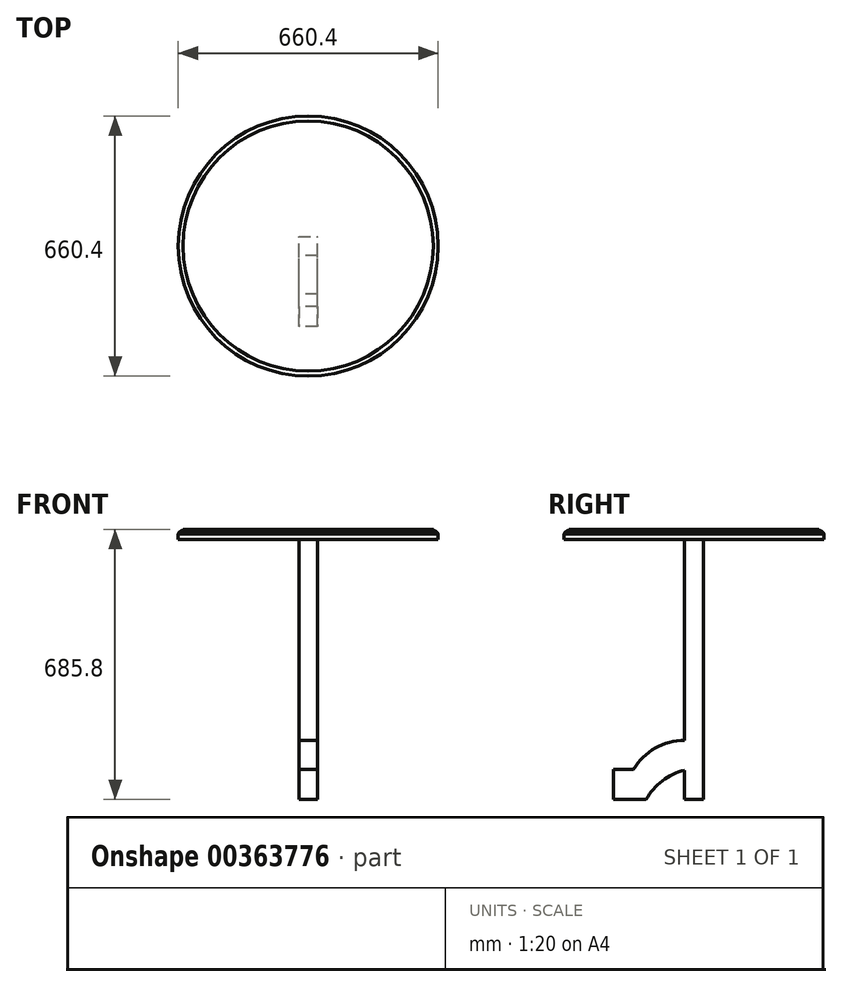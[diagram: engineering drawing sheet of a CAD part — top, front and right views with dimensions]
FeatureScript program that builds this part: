
annotation { "Feature Type Name" : "Feature", "Feature Type Description" : "" }
export const myFeature = defineFeature(function(context is Context, id is Id, definition is map)
    precondition{}
    {
        {
            var Q0;
            Q0=qCreatedBy(makeId("Top.planeOp"),FACE);
            var sketch = newSketch(context, id + "F0", { "sketchPlane" : qUnion([Q0])});
            skCircle(sketch, "E0", {"center": v(0, 0) * mm, "radius": 330.2 * mm});
            skSolve(sketch);
        }
        {
            var Q0;
            Q0=makeQuery(id+"F0.imprint","IMPRINT",FACE,{"disambiguationData":[TD([[makeQuery(id+"F0.imprint","IMPRINT",EDGE,{"derivedFrom":sQuery(id+"F0.wireOp",EDGE,"E0")}),1.0]])]});
            extrude(context, id + "F1", {"entities" : qUnion([Q0]), "depth" : 25.4 * mm});
        }
        {
            var Q0;
            Q0=qCreatedBy(makeId("Front.planeOp"),FACE);
            var sketch = newSketch(context, id + "F2", { "sketchPlane" : qUnion([Q0])});
            skLineSegment(sketch, "E1", {"start": v(-317.8, 25.4) * mm, "end": v(-317.8, 22.86) * mm});
            skArc(sketch, "E2", {"start": v(-317.8, 22.86) * mm, "mid": v(-325.99, 20.08) * mm, "end": v(-330.5, 12.7) * mm});
            skLineSegment(sketch, "E3", {"start": v(-330.5, 12.7) * mm, "end": v(-330.5, 25.4) * mm});
            skLineSegment(sketch, "E4", {"start": v(-330.5, 25.4) * mm, "end": v(-317.8, 25.4) * mm});
            skLineSegment(sketch, "E5", {"start": v(0, 84.6) * mm, "end": v(0, -114.4) * mm, "construction": true});
            skSolve(sketch);
        }
        {
            var Q0;
            Q0=makeQuery(id+"F2.imprint","IMPRINT",FACE,{"disambiguationData":[TD([[makeQuery(id+"F2.imprint","IMPRINT",EDGE,{"derivedFrom":sQuery(id+"F2.wireOp",EDGE,"E1")}),-1.0]])]});
            var Q1;
            Q1=sQuery(id+"F2.wireOp",EDGE,"E5");
            revolve(context, id + "F3", {"operationType" : NewBodyOperationType.REMOVE, "entities" : qUnion([Q0]), "axis" : qUnion([Q1]), "revolveType" : RevolveType.FULL, "oppositeDirection" : true});
        }
        {
            var Q0;
            Q0=makeQuery(id+"F1.opExtrude","CAP_FACE",FACE,{"disambiguationData":[OSD([sQuery(id+"F0.wireOp",EDGE,"E0")])],"isStart":true});
            var sketch = newSketch(context, id + "F4", { "sketchPlane" : qUnion([Q0])});
            skLineSegment(sketch, "E6.bottom", {"start": v(-23.81, 23.81) * mm, "end": v(23.81, 23.81) * mm});
            skLineSegment(sketch, "E6.top", {"start": v(-23.81, -23.81) * mm, "end": v(23.81, -23.81) * mm});
            skLineSegment(sketch, "E6.left", {"start": v(-23.81, 23.81) * mm, "end": v(-23.81, -23.81) * mm});
            skLineSegment(sketch, "E6.right", {"start": v(23.81, 23.81) * mm, "end": v(23.81, -23.81) * mm});
            skLineSegment(sketch, "E7", {"start": v(-23.81, 23.81) * mm, "end": v(23.81, -23.81) * mm, "construction": true});
            skPoint(sketch, "E8", {"position": v(0, 0) * mm});
            skSolve(sketch);
        }
        {
            var Q0;
            Q0 = qSketchRegion(id + "F4", true);
            extrude(context, id + "F5", {"entities" : qUnion([Q0]), "operationType" : NewBodyOperationType.ADD, "depth" : 660.4 * mm});
        }
        {
            var Q0;
            Q0=makeQuery(id+"F5.opExtrude","SWEPT_FACE",FACE,{"disambiguationData":[OSD([sQuery(id+"F4.wireOp",EDGE,"E6.left")])]});
            var sketch = newSketch(context, id + "F6", { "sketchPlane" : qUnion([Q0])});
            skArc(sketch, "E9", {"start": v(153.35, -584.2) * mm, "mid": v(98.43, -529.94) * mm, "end": v(23.81, -510.11) * mm});
            skLineSegment(sketch, "E10", {"start": v(153.35, -584.2) * mm, "end": v(204.15, -584.2) * mm});
            skLineSegment(sketch, "E11", {"start": v(204.15, -584.2) * mm, "end": v(204.15, -660.4) * mm});
            skLineSegment(sketch, "E12", {"start": v(204.15, -660.4) * mm, "end": v(121.6, -660.4) * mm});
            skArc(sketch, "E13", {"start": v(121.6, -660.4) * mm, "mid": v(80.61, -612.92) * mm, "end": v(23.81, -586.31) * mm});
            skLineSegment(sketch, "E14", {"start": v(23.81, -586.31) * mm, "end": v(23.81, -510.11) * mm});
            skLineSegment(sketch, "E15", {"start": v(23.81, -510.11) * mm, "end": v(57.77, -510.11) * mm, "construction": true});
            skSolve(sketch);
        }
        {
            var Q0;
            Q0=makeQuery(id+"F6.imprint","IMPRINT",FACE,{"disambiguationData":[TD([[makeQuery(id+"F6.imprint","IMPRINT",EDGE,{"derivedFrom":sQuery(id+"F6.wireOp",EDGE,"E9")}),1.0]])]});
            extrude(context, id + "F7", {"entities" : qUnion([Q0]), "operationType" : NewBodyOperationType.ADD, "oppositeDirection" : true, "depth" : 47.62 * mm});
        }
    });
